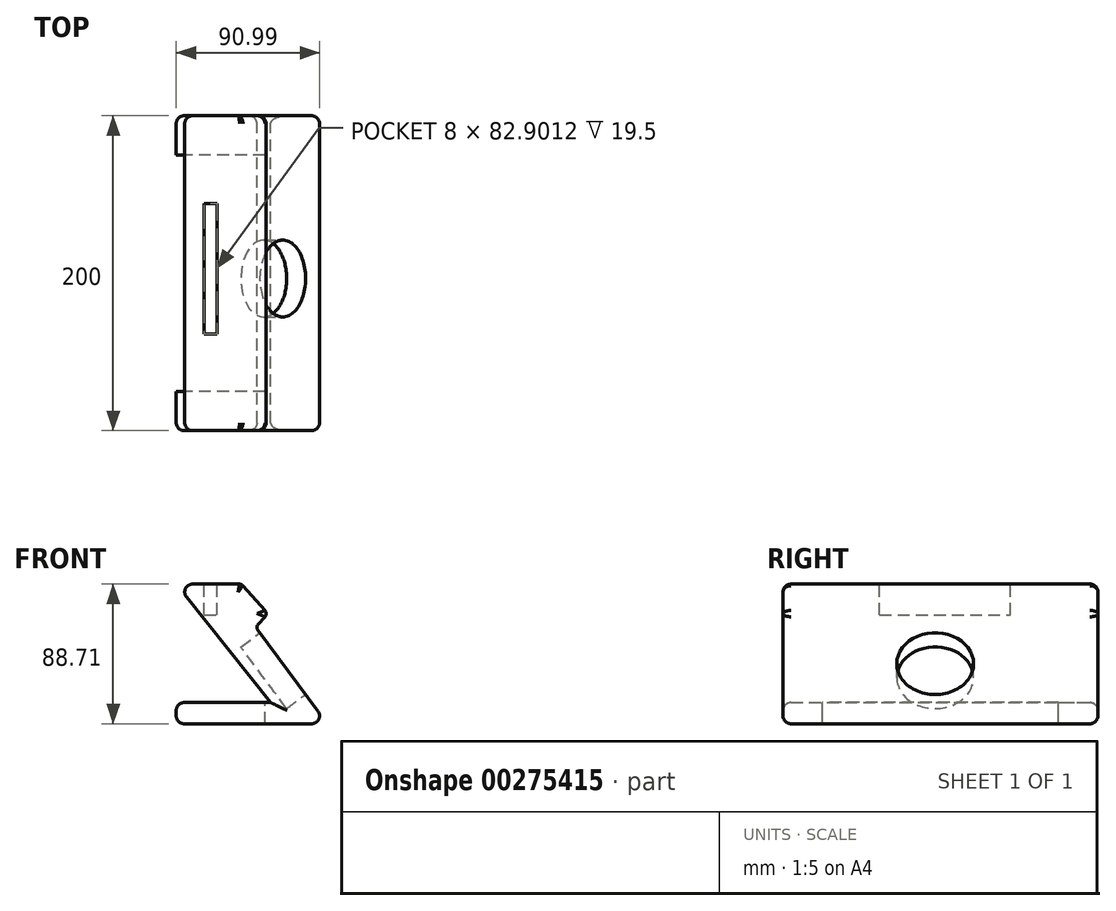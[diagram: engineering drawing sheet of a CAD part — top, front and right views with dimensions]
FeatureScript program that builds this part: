
annotation { "Feature Type Name" : "Feature", "Feature Type Description" : "" }
export const myFeature = defineFeature(function(context is Context, id is Id, definition is map)
    precondition{}
    {
        {
            var Q0;
            Q0=qCreatedBy(makeId("Front.planeOp"),FACE);
            var sketch = newSketch(context, id + "F0", { "sketchPlane" : qUnion([Q0])});
            skLineSegment(sketch, "E0.bottom", {"start": v(-12.37, 45.3) * mm, "end": v(0, 45.3) * mm});
            skLineSegment(sketch, "E0.left", {"start": v(-22.75, -29.92) * mm, "end": v(-22.75, -43.4) * mm});
            skLineSegment(sketch, "E1", {"start": v(-16.27, 37.19) * mm, "end": v(37.25, -29.92) * mm});
            skLineSegment(sketch, "E2", {"start": v(37.25, -29.92) * mm, "end": v(-17.75, -29.92) * mm});
            skLineSegment(sketch, "E3", {"start": v(-22.75, -34.92) * mm, "end": v(-22.75, -38.4) * mm});
            skLineSegment(sketch, "E4", {"start": v(-17.75, -43.4) * mm, "end": v(63.24, -43.4) * mm});
            skPoint(sketch, "E5.end.orphan", {"position": v(0, 45.3) * mm});
            skPoint(sketch, "E6.visualSharp", {"position": v(72.78, -43.4) * mm});
            skArc(sketch, "E6.filletArc", {"start": v(63.24, -43.4) * mm, "mid": v(67.7, -40.65) * mm, "end": v(67.25, -35.42) * mm});
            skPoint(sketch, "E7.visualSharp", {"position": v(-22.75, -43.4) * mm});
            skArc(sketch, "E7.filletArc", {"start": v(-22.75, -38.4) * mm, "mid": v(-21.28, -41.94) * mm, "end": v(-17.75, -43.4) * mm});
            skPoint(sketch, "E8.visualSharp", {"position": v(-22.75, -29.92) * mm});
            skArc(sketch, "E8.filletArc", {"start": v(-17.75, -29.92) * mm, "mid": v(-21.28, -31.38) * mm, "end": v(-22.75, -34.92) * mm});
            skLineSegment(sketch, "E9", {"start": v(67.25, -35.42) * mm, "end": v(29.07, 16.03) * mm});
            skPoint(sketch, "E10.visualSharp", {"position": v(-22.75, 45.3) * mm});
            skArc(sketch, "E10.filletArc", {"start": v(-12.37, 45.3) * mm, "mid": v(-16.87, 42.48) * mm, "end": v(-16.27, 37.19) * mm});
            skLineSegment(sketch, "E11", {"start": v(0, 45.3) * mm, "end": v(17.38, 45.3) * mm});
            skLineSegment(sketch, "E12", {"start": v(19.62, 44.3) * mm, "end": v(33.59, 28.56) * mm});
            skLineSegment(sketch, "E13", {"start": v(33.56, 24.54) * mm, "end": v(29.27, 19.84) * mm});
            skPoint(sketch, "E14.visualSharp", {"position": v(18.73, 45.3) * mm});
            skArc(sketch, "E14.filletArc", {"start": v(19.62, 44.3) * mm, "mid": v(18.6, 45.04) * mm, "end": v(17.38, 45.3) * mm});
            skPoint(sketch, "E15.visualSharp", {"position": v(35.38, 26.54) * mm});
            skArc(sketch, "E15.filletArc", {"start": v(33.56, 24.54) * mm, "mid": v(34.34, 26.54) * mm, "end": v(33.59, 28.56) * mm});
            skPoint(sketch, "E16.visualSharp", {"position": v(27.6, 18.01) * mm});
            skArc(sketch, "E16.filletArc", {"start": v(29.27, 19.84) * mm, "mid": v(28.49, 17.97) * mm, "end": v(29.07, 16.03) * mm});
            skSolve(sketch);
        }
        {
            var Q0;
            Q0=qSketchRegion(id+"F0",true);
            extrude(context, id + "F1", {"entities" : qUnion([Q0]), "depth" : 200 * mm});
        }
        {
            var Q0;
            Q0=makeQuery(id+"F1.opExtrude","SWEPT_FACE",FACE,{"disambiguationData":[OSD([sQuery(id+"F0.wireOp",EDGE,"E0.bottom"),sQuery(id+"F0.wireOp",EDGE,"E11")])]});
            var sketch = newSketch(context, id + "F2", { "sketchPlane" : qUnion([Q0])});
            skLineSegment(sketch, "E17.bottom", {"start": v(-4.98, -138.64) * mm, "end": v(3.02, -138.64) * mm});
            skLineSegment(sketch, "E17.top", {"start": v(-4.98, -55.74) * mm, "end": v(3.02, -55.74) * mm});
            skLineSegment(sketch, "E17.left", {"start": v(-4.98, -138.64) * mm, "end": v(-4.98, -55.74) * mm});
            skLineSegment(sketch, "E17.right", {"start": v(3.02, -138.64) * mm, "end": v(3.02, -55.74) * mm});
            skSolve(sketch);
        }
        {
            var Q0;
            Q0=makeQuery(id+"F2.imprint","IMPRINT",FACE,{"disambiguationData":[TD([[makeQuery(id+"F2.imprint","IMPRINT",EDGE,{"derivedFrom":sQuery(id+"F2.wireOp",EDGE,"E17.bottom")}),1.0]])]});
            extrude(context, id + "F3", {"entities" : qUnion([Q0]), "operationType" : NewBodyOperationType.REMOVE, "oppositeDirection" : true, "depth" : 19.5 * mm});
        }
        {
            var Q0;
            Q0=makeQuery(id+"F1.opExtrude","SWEPT_FACE",FACE,{"disambiguationData":[OSD([sQuery(id+"F0.wireOp",EDGE,"E9")])]});
            var sketch = newSketch(context, id + "F4", { "sketchPlane" : qUnion([Q0])});
            skCircle(sketch, "E18", {"center": v(-103.38, -30.94) * mm, "radius": 24.4 * mm});
            skSolve(sketch);
        }
        {
            var Q0;
            Q0=makeQuery(id+"F4.imprint","IMPRINT",FACE,{"disambiguationData":[TD([[makeQuery(id+"F4.imprint","IMPRINT",EDGE,{"derivedFrom":sQuery(id+"F4.wireOp",EDGE,"E18")}),1.0]])]});
            extrude(context, id + "F5", {"entities" : qUnion([Q0]), "operationType" : NewBodyOperationType.REMOVE, "oppositeDirection" : true, "depth" : 15 * mm});
        }
        {
            var Q0;
            Q0=makeQuery(id+"F1.opExtrude","CAP_EDGE",EDGE,{"disambiguationData":[OSD([sQuery(id+"F0.wireOp",EDGE,"E9")])],"isStart":false});
            var Q1;
            Q1=makeQuery(id+"F1.opExtrude","CAP_EDGE",EDGE,{"disambiguationData":[OSD([sQuery(id+"F0.wireOp",EDGE,"E9")])],"isStart":true});
            fillet(context, id + "F6", {"entities" : qUnion([Q0, Q1]), "radius" : 5 * mm, "tangentPropagation" : true, "allowEdgeOverflow" : false});
        }
        {
            var Q0;
            Q0=makeQuery(id+"F1.opExtrude","SWEPT_FACE",FACE,{"disambiguationData":[OSD([sQuery(id+"F0.wireOp",EDGE,"E2")])]});
            var sketch = newSketch(context, id + "F7", { "sketchPlane" : qUnion([Q0])});
            skLineSegment(sketch, "E19.bottom", {"start": v(33.64, -25) * mm, "end": v(-35.2, -25) * mm});
            skLineSegment(sketch, "E19.top", {"start": v(33.64, -175) * mm, "end": v(-35.2, -175) * mm});
            skLineSegment(sketch, "E19.left", {"start": v(33.64, -25) * mm, "end": v(33.64, -175) * mm});
            skLineSegment(sketch, "E19.right", {"start": v(-35.2, -25) * mm, "end": v(-35.2, -175) * mm});
            skSolve(sketch);
        }
        {
            var Q0;
            {var subQ0=sQuery(id+"F7.wireOp",EDGE,"E19.left");Q0=makeQuery(id+"F7.imprint","IMPRINT",FACE,{"disambiguationData":[TD([[makeQuery(id+"F7.imprint","IMPRINT",EDGE,{"derivedFrom":subQ0}),-1.0]])]});}
            var Q1;
            Q1 = qSketchRegion(id + "F7", true);
            extrude(context, id + "F8", {"entities" : qUnion([Q0, Q1]), "operationType" : NewBodyOperationType.REMOVE, "oppositeDirection" : true, "depth" : 25 * mm});
        }
    });
